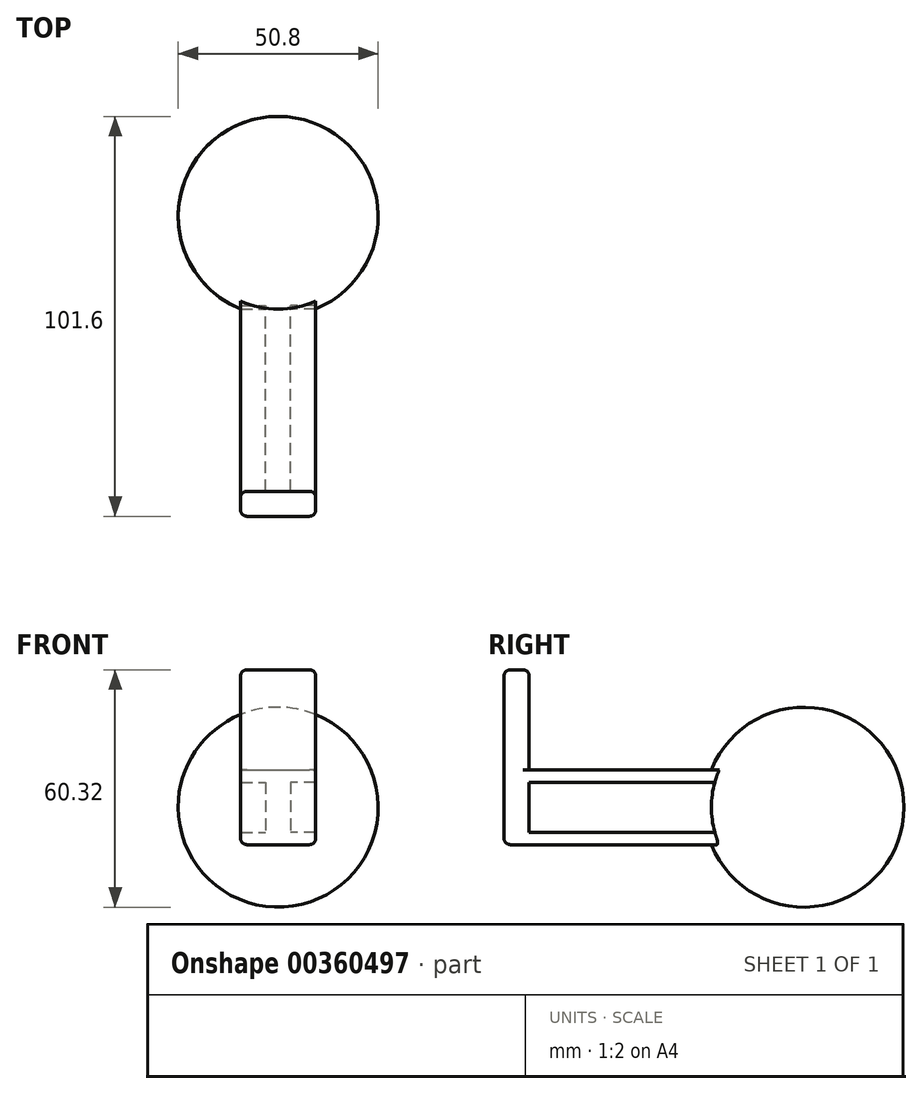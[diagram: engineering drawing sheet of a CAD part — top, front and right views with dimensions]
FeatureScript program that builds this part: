
annotation { "Feature Type Name" : "Feature", "Feature Type Description" : "" }
export const myFeature = defineFeature(function(context is Context, id is Id, definition is map)
    precondition{}
    {
        {
            var Q0;
            Q0=qCreatedBy(makeId("Top.planeOp"),FACE);
            var sketch = newSketch(context, id + "F0", { "sketchPlane" : qUnion([Q0])});
            skCircle(sketch, "E0", {"center": v(0, 0) * mm, "radius": 25.4 * mm});
            skLineSegment(sketch, "E1", {"start": v(0, 25.4) * mm, "end": v(0, -46.14) * mm});
            skLineSegment(sketch, "E2", {"start": v(0, -46.14) * mm, "end": v(0, 44.48) * mm});
            skSolve(sketch);
        }
        {
            var Q0;
            {var subQ0=sQuery(id+"F0.wireOp",EDGE,"E2");var subQ1=sQuery(id+"F0.wireOp",EDGE,"E0");var subQ2=makeQuery(id+"F0.imprint","INTERSECT",VERTEX,{"disambiguationData":[OD(0.0)],"derivedFrom":[subQ1,subQ0]});Q0=makeQuery(id+"F0.imprint","IMPRINT",FACE,{"disambiguationData":[TD([[makeQuery(id+"F0.imprint","IMPRINT",EDGE,{"disambiguationData":[TD([[subQ2,-1.0]])],"derivedFrom":subQ1}),1.0]])]});}
            var Q1;
            Q1=sQuery(id+"F0.wireOp",EDGE,"E2");
            revolve(context, id + "F1", {"entities" : qUnion([Q0]), "axis" : qUnion([Q1]), "revolveType" : RevolveType.FULL});
        }
        {
            var Q0;
            Q0=qCreatedBy(makeId("Front.planeOp"),FACE);
            var sketch = newSketch(context, id + "F2", { "sketchPlane" : qUnion([Q0])});
            skLineSegment(sketch, "E3.bottom", {"start": v(-9.53, 9.53) * mm, "end": v(9.53, 9.53) * mm});
            skLineSegment(sketch, "E3.top", {"start": v(-9.53, -9.53) * mm, "end": v(9.53, -9.53) * mm});
            skLineSegment(sketch, "E3.left", {"start": v(-9.53, 9.52) * mm, "end": v(-9.53, -9.53) * mm});
            skLineSegment(sketch, "E3.right", {"start": v(9.52, 9.52) * mm, "end": v(9.53, -9.52) * mm});
            skPoint(sketch, "E4", {"position": v(0, -9.53) * mm});
            skPoint(sketch, "E5", {"position": v(9.53, 0) * mm});
            skSolve(sketch);
        }
        {
            var Q0;
            Q0=makeQuery(id+"F2.imprint","IMPRINT",FACE,{"disambiguationData":[TD([[makeQuery(id+"F2.imprint","IMPRINT",EDGE,{"derivedFrom":sQuery(id+"F2.wireOp",EDGE,"E3.bottom")}),-1.0]])]});
            extrude(context, id + "F3", {"entities" : qUnion([Q0]), "operationType" : NewBodyOperationType.ADD, "depth" : 76.2 * mm});
        }
        {
            var Q0;
            Q0=makeQuery(id+"F3.opExtrude","SWEPT_FACE",FACE,{"disambiguationData":[OSD([sQuery(id+"F2.wireOp",EDGE,"E3.bottom")])]});
            var sketch = newSketch(context, id + "F4", { "sketchPlane" : qUnion([Q0])});
            skLineSegment(sketch, "E6.bottom", {"start": v(-9.53, -76.2) * mm, "end": v(9.53, -76.2) * mm});
            skLineSegment(sketch, "E6.top", {"start": v(-9.53, -69.85) * mm, "end": v(9.53, -69.85) * mm});
            skLineSegment(sketch, "E6.left", {"start": v(-9.53, -76.2) * mm, "end": v(-9.53, -69.85) * mm});
            skLineSegment(sketch, "E6.right", {"start": v(9.53, -76.2) * mm, "end": v(9.53, -69.85) * mm});
            skSolve(sketch);
        }
        {
            var Q0;
            Q0 = qSketchRegion(id + "F4", true);
            extrude(context, id + "F5", {"entities" : qUnion([Q0]), "operationType" : NewBodyOperationType.ADD, "depth" : 25.4 * mm});
        }
        {
            var Q0;
            Q0=makeQuery(id+"F5.boolean.opBoolean","MERGE",FACE,{"derivedFrom":[makeQuery(id+"F3.opExtrude","SWEPT_FACE",FACE,{"disambiguationData":[OSD([sQuery(id+"F2.wireOp",EDGE,"E3.right")])]}),makeQuery(id+"F5.opExtrude","SWEPT_FACE",FACE,{"disambiguationData":[OSD([sQuery(id+"F4.wireOp",EDGE,"E6.right")])]})]});
            var sketch = newSketch(context, id + "F6", { "sketchPlane" : qUnion([Q0])});
            skLineSegment(sketch, "E7.0", {"start": v(-69.85, 6.35) * mm, "end": v(-22.67, 6.35) * mm});
            skLineSegment(sketch, "E8.0", {"start": v(-69.85, -6.35) * mm, "end": v(-22.67, -6.35) * mm});
            skLineSegment(sketch, "E9.0", {"start": v(-69.85, 6.35) * mm, "end": v(-69.85, -6.35) * mm});
            skArc(sketch, "E10", {"start": v(-22.67, 6.35) * mm, "mid": v(-23.55, 0) * mm, "end": v(-22.67, -6.35) * mm});
            skSolve(sketch);
        }
        {
            var Q0;
            Q0=makeQuery(id+"F6.imprint","IMPRINT",FACE,{"disambiguationData":[TD([[makeQuery(id+"F6.imprint","IMPRINT",EDGE,{"derivedFrom":sQuery(id+"F6.wireOp",EDGE,"E7.0")}),-1.0]])]});
            extrude(context, id + "F7", {"entities" : qUnion([Q0]), "endBound" : BoundingType.SYMMETRIC, "depth" : 12.7 * mm});
        }
        {
            var Q0;
            Q0=makeQuery(id+"F7.opExtrude","SWEPT_BODY",BODY,{"disambiguationData":[OSD([sQuery(id+"F6.wireOp",EDGE,"E7.0"),sQuery(id+"F6.wireOp",EDGE,"E8.0"),sQuery(id+"F6.wireOp",EDGE,"E9.0"),sQuery(id+"F6.wireOp",EDGE,"E10")])]});
            var Q1;
            Q1=qCreatedBy(makeId("Right.planeOp"),FACE);
            mirror(context, id + "F8", {"entities" : qUnion([Q0]), "mirrorPlane" : qUnion([Q1])});
        }
        {
            var Q0;
            Q0=makeQuery(id+"F8.opPattern","COPY",BODY,{"derivedFrom":makeQuery(id+"F7.opExtrude","SWEPT_BODY",BODY,{"disambiguationData":[OSD([sQuery(id+"F6.wireOp",EDGE,"E7.0"),sQuery(id+"F6.wireOp",EDGE,"E8.0"),sQuery(id+"F6.wireOp",EDGE,"E9.0"),sQuery(id+"F6.wireOp",EDGE,"E10")])]}),"instanceName":"1"});
            var Q1;
            Q1=makeQuery(id+"F7.opExtrude","SWEPT_BODY",BODY,{"disambiguationData":[OSD([sQuery(id+"F6.wireOp",EDGE,"E7.0"),sQuery(id+"F6.wireOp",EDGE,"E8.0"),sQuery(id+"F6.wireOp",EDGE,"E9.0"),sQuery(id+"F6.wireOp",EDGE,"E10")])]});
            var Q2;
            Q2=makeQuery(id+"F1.opRevolve","SWEPT_BODY",BODY,{"disambiguationData":[OSD([sQuery(id+"F0.wireOp",EDGE,"E0"),sQuery(id+"F0.wireOp",EDGE,"E2")])]});
            booleanBodies(context, id + "F9", {"operationType" : BooleanOperationType.SUBTRACTION, "tools" : qUnion([Q0, Q1]), "targets" : qUnion([Q2])});
        }
        {
            var Q0;
            Q0=makeQuery(id+"F5.opExtrude","CAP_EDGE",EDGE,{"disambiguationData":[OSD([sQuery(id+"F4.wireOp",EDGE,"E6.bottom")])],"isStart":false});
            var Q1;
            Q1=makeQuery(id+"F5.opExtrude","CAP_EDGE",EDGE,{"disambiguationData":[OSD([sQuery(id+"F4.wireOp",EDGE,"E6.right")])],"isStart":false});
            var Q2;
            Q2=makeQuery(id+"F5.opExtrude","CAP_EDGE",EDGE,{"disambiguationData":[OSD([sQuery(id+"F4.wireOp",EDGE,"E6.top")])],"isStart":false});
            var Q3;
            Q3=makeQuery(id+"F5.opExtrude","CAP_EDGE",EDGE,{"disambiguationData":[OSD([sQuery(id+"F4.wireOp",EDGE,"E6.left")])],"isStart":false});
            var Q4;
            Q4=makeQuery(id+"F5.boolean.opBoolean","MERGE",EDGE,{"derivedFrom":[makeQuery(id+"F3.opExtrude","CAP_EDGE",EDGE,{"disambiguationData":[OSD([sQuery(id+"F2.wireOp",EDGE,"E3.right")])],"isStart":false}),makeQuery(id+"F5.opExtrude","SWEPT_EDGE",EDGE,{"disambiguationData":[OSD([sQuery(id+"F4.wireOp",EDGE,"E6.bottom"),sQuery(id+"F4.wireOp",EDGE,"E6.right")])]})]});
            var Q5;
            Q5=makeQuery(id+"F5.boolean.opBoolean","MERGE",EDGE,{"derivedFrom":[makeQuery(id+"F3.opExtrude","CAP_EDGE",EDGE,{"disambiguationData":[OSD([sQuery(id+"F2.wireOp",EDGE,"E3.left")])],"isStart":false}),makeQuery(id+"F5.opExtrude","SWEPT_EDGE",EDGE,{"disambiguationData":[OSD([sQuery(id+"F4.wireOp",EDGE,"E6.bottom"),sQuery(id+"F4.wireOp",EDGE,"E6.left")])]})]});
            var Q6;
            Q6=makeQuery(id+"F5.opExtrude","SWEPT_EDGE",EDGE,{"disambiguationData":[OSD([sQuery(id+"F2.wireOp",EDGE,"E3.bottom"),sQuery(id+"F2.wireOp",EDGE,"E3.left"),sQuery(id+"F4.wireOp",EDGE,"E6.top"),sQuery(id+"F4.wireOp",EDGE,"E6.left")])]});
            var Q7;
            Q7=makeQuery(id+"F5.opExtrude","SWEPT_EDGE",EDGE,{"disambiguationData":[OSD([sQuery(id+"F2.wireOp",EDGE,"E3.bottom"),sQuery(id+"F2.wireOp",EDGE,"E3.right"),sQuery(id+"F4.wireOp",EDGE,"E6.top"),sQuery(id+"F4.wireOp",EDGE,"E6.right")])]});
            var Q8;
            Q8=makeQuery(id+"F3.opExtrude","CAP_EDGE",EDGE,{"disambiguationData":[OSD([sQuery(id+"F2.wireOp",EDGE,"E3.top")])],"isStart":false});
            var Q9;
            Q9=makeQuery(id+"F5.opExtrude","CAP_EDGE",EDGE,{"disambiguationData":[OSD([sQuery(id+"F4.wireOp",EDGE,"E6.top")])],"isStart":true});
            var Q10;
            Q10=makeQuery(id+"F3.opExtrude","SWEPT_EDGE",EDGE,{"disambiguationData":[OSD([sQuery(id+"F2.wireOp",EDGE,"E3.top"),sQuery(id+"F2.wireOp",EDGE,"E3.right")])]});
            var Q11;
            Q11=makeQuery(id+"F3.opExtrude","SWEPT_EDGE",EDGE,{"disambiguationData":[OSD([sQuery(id+"F2.wireOp",EDGE,"E3.top"),sQuery(id+"F2.wireOp",EDGE,"E3.left")])]});
            fillet(context, id + "F10", {"entities" : qUnion([Q0, Q1, Q2, Q3, Q4, Q5, Q6, Q7, Q8, Q9, Q10, Q11]), "radius" : 1.59 * mm, "tangentPropagation" : true, "allowEdgeOverflow" : false});
        }
    });
